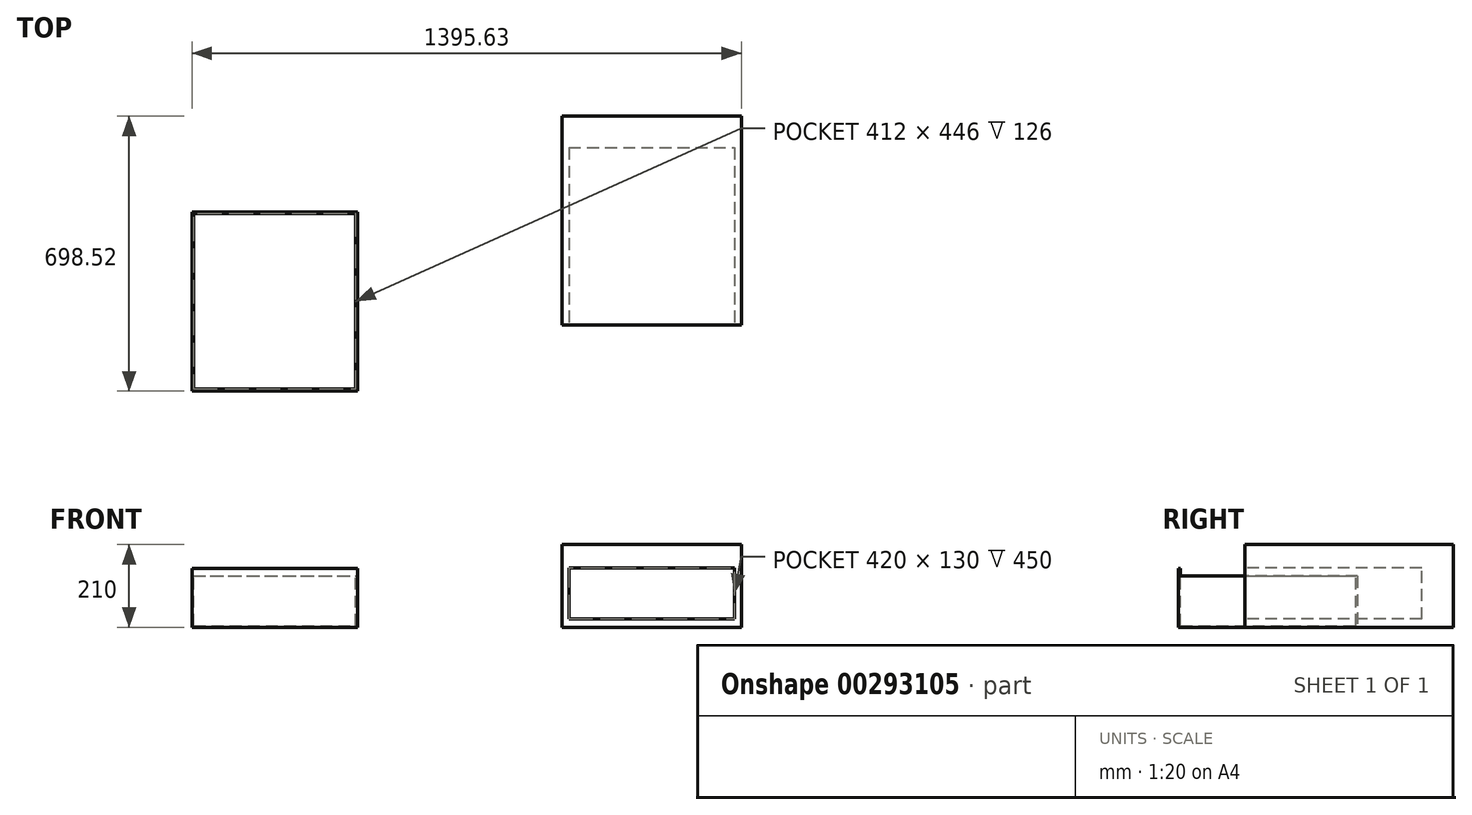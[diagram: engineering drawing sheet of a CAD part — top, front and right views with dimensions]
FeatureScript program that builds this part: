
annotation { "Feature Type Name" : "Feature", "Feature Type Description" : "" }
export const myFeature = defineFeature(function(context is Context, id is Id, definition is map)
    precondition{}
    {
        {
            var Q0;
            Q0=qCreatedBy(makeId("Top.planeOp"),FACE);
            var sketch = newSketch(context, id + "F0", { "sketchPlane" : qUnion([Q0])});
            skLineSegment(sketch, "E0.bottom", {"start": v(228, 265) * mm, "end": v(-228, 265) * mm});
            skLineSegment(sketch, "E0.top", {"start": v(228, -265) * mm, "end": v(-228, -265) * mm});
            skLineSegment(sketch, "E0.left", {"start": v(228, 265) * mm, "end": v(228, -265) * mm});
            skLineSegment(sketch, "E0.right", {"start": v(-228, 265) * mm, "end": v(-228, -265) * mm});
            skPoint(sketch, "E0.middle", {"position": v(0, 0) * mm});
            skSolve(sketch);
        }
        {
            var Q0;
            Q0=makeQuery(id+"F0.imprint","IMPRINT",FACE,{"disambiguationData":[TD([[makeQuery(id+"F0.imprint","IMPRINT",EDGE,{"derivedFrom":sQuery(id+"F0.wireOp",EDGE,"E0.bottom")}),1.0]])]});
            extrude(context, id + "F1", {"entities" : qUnion([Q0]), "depth" : 210 * mm});
        }
        {
            var Q0;
            Q0=makeQuery(id+"F1.opExtrude","SWEPT_FACE",FACE,{"disambiguationData":[OSD([sQuery(id+"F0.wireOp",EDGE,"E0.top")])]});
            var sketch = newSketch(context, id + "F2", { "sketchPlane" : qUnion([Q0])});
            skLineSegment(sketch, "E1.bottom", {"start": v(-210, 21) * mm, "end": v(210, 21) * mm});
            skLineSegment(sketch, "E1.top", {"start": v(-210, 151) * mm, "end": v(210, 151) * mm});
            skLineSegment(sketch, "E1.left", {"start": v(-210, 21) * mm, "end": v(-210, 151) * mm});
            skLineSegment(sketch, "E1.right", {"start": v(210, 21) * mm, "end": v(210, 151) * mm});
            skSolve(sketch);
        }
        {
            var Q0;
            Q0=makeQuery(id+"F2.imprint","IMPRINT",FACE,{"disambiguationData":[TD([[makeQuery(id+"F2.imprint","IMPRINT",EDGE,{"derivedFrom":sQuery(id+"F2.wireOp",EDGE,"E1.bottom")}),1.0]])]});
            extrude(context, id + "F3", {"entities" : qUnion([Q0]), "operationType" : NewBodyOperationType.REMOVE, "oppositeDirection" : true, "depth" : 450 * mm});
        }
        {
            var Q0;
            Q0=qCreatedBy(makeId("Top.planeOp"),FACE);
            var sketch = newSketch(context, id + "F4", { "sketchPlane" : qUnion([Q0])});
            skLineSegment(sketch, "E2.bottom", {"start": v(-1167.63, 21.48) * mm, "end": v(-747.63, 21.48) * mm});
            skLineSegment(sketch, "E2.top", {"start": v(-1167.63, -428.52) * mm, "end": v(-747.63, -428.52) * mm});
            skLineSegment(sketch, "E2.left", {"start": v(-1167.63, 21.48) * mm, "end": v(-1167.63, -428.52) * mm});
            skLineSegment(sketch, "E2.right", {"start": v(-747.63, 21.48) * mm, "end": v(-747.63, -428.52) * mm});
            skSolve(sketch);
        }
        {
            var Q0;
            Q0=makeQuery(id+"F4.imprint","IMPRINT",FACE,{"disambiguationData":[TD([[makeQuery(id+"F4.imprint","IMPRINT",EDGE,{"derivedFrom":sQuery(id+"F4.wireOp",EDGE,"E2.bottom")}),-1.0]])]});
            extrude(context, id + "F5", {"entities" : qUnion([Q0]), "depth" : 130 * mm});
        }
        {
            var Q0;
            Q0=makeQuery(id+"F5.opExtrude","CAP_FACE",FACE,{"disambiguationData":[OSD([sQuery(id+"F4.wireOp",EDGE,"E2.bottom"),sQuery(id+"F4.wireOp",EDGE,"E2.top"),sQuery(id+"F4.wireOp",EDGE,"E2.left"),sQuery(id+"F4.wireOp",EDGE,"E2.right")])],"isStart":false});
            var sketch = newSketch(context, id + "F6", { "sketchPlane" : qUnion([Q0])});
            skLineSegment(sketch, "E3.bottom", {"start": v(-1163.63, -428.52) * mm, "end": v(-751.63, -428.52) * mm});
            skLineSegment(sketch, "E3.top", {"start": v(-1163.63, 17.48) * mm, "end": v(-751.63, 17.48) * mm});
            skLineSegment(sketch, "E3.left", {"start": v(-1163.63, -428.52) * mm, "end": v(-1163.63, 17.48) * mm});
            skLineSegment(sketch, "E3.right", {"start": v(-751.63, -428.52) * mm, "end": v(-751.63, 17.48) * mm});
            skSolve(sketch);
        }
        {
            var Q0;
            Q0=makeQuery(id+"F6.imprint","IMPRINT",FACE,{"disambiguationData":[TD([[makeQuery(id+"F6.imprint","IMPRINT",EDGE,{"derivedFrom":sQuery(id+"F6.wireOp",EDGE,"E3.bottom")}),1.0]])]});
            extrude(context, id + "F7", {"entities" : qUnion([Q0]), "operationType" : NewBodyOperationType.REMOVE, "oppositeDirection" : true, "depth" : 126 * mm});
        }
        {
            var Q0;
            Q0=makeQuery(id+"F5.opExtrude","SWEPT_FACE",FACE,{"disambiguationData":[OSD([sQuery(id+"F4.wireOp",EDGE,"E2.top")])]});
            var sketch = newSketch(context, id + "F8", { "sketchPlane" : qUnion([Q0])});
            skLineSegment(sketch, "E4.bottom", {"start": v(-1167.63, 0) * mm, "end": v(-747.63, 0) * mm});
            skLineSegment(sketch, "E4.top", {"start": v(-1167.63, 150) * mm, "end": v(-747.63, 150) * mm});
            skLineSegment(sketch, "E4.left", {"start": v(-1167.63, 0) * mm, "end": v(-1167.63, 150) * mm});
            skLineSegment(sketch, "E4.right", {"start": v(-747.63, 0) * mm, "end": v(-747.63, 150) * mm});
            skSolve(sketch);
        }
        {
            var Q0;
            {var subQ0=sQuery(id+"F8.wireOp",EDGE,"E4.bottom");Q0=makeQuery(id+"F8.imprint","IMPRINT",FACE,{"disambiguationData":[TD([[makeQuery(id+"F8.imprint","IMPRINT",EDGE,{"derivedFrom":subQ0}),1.0]])]});}
            var Q1;
            {var subQ0=sQuery(id+"F8.wireOp",EDGE,"E4.top");Q1=makeQuery(id+"F8.imprint","IMPRINT",FACE,{"disambiguationData":[TD([[makeQuery(id+"F8.imprint","IMPRINT",EDGE,{"derivedFrom":subQ0}),-1.0]])]});}
            extrude(context, id + "F9", {"entities" : qUnion([Q0, Q1]), "operationType" : NewBodyOperationType.ADD, "depth" : 5 * mm});
        }
    });
